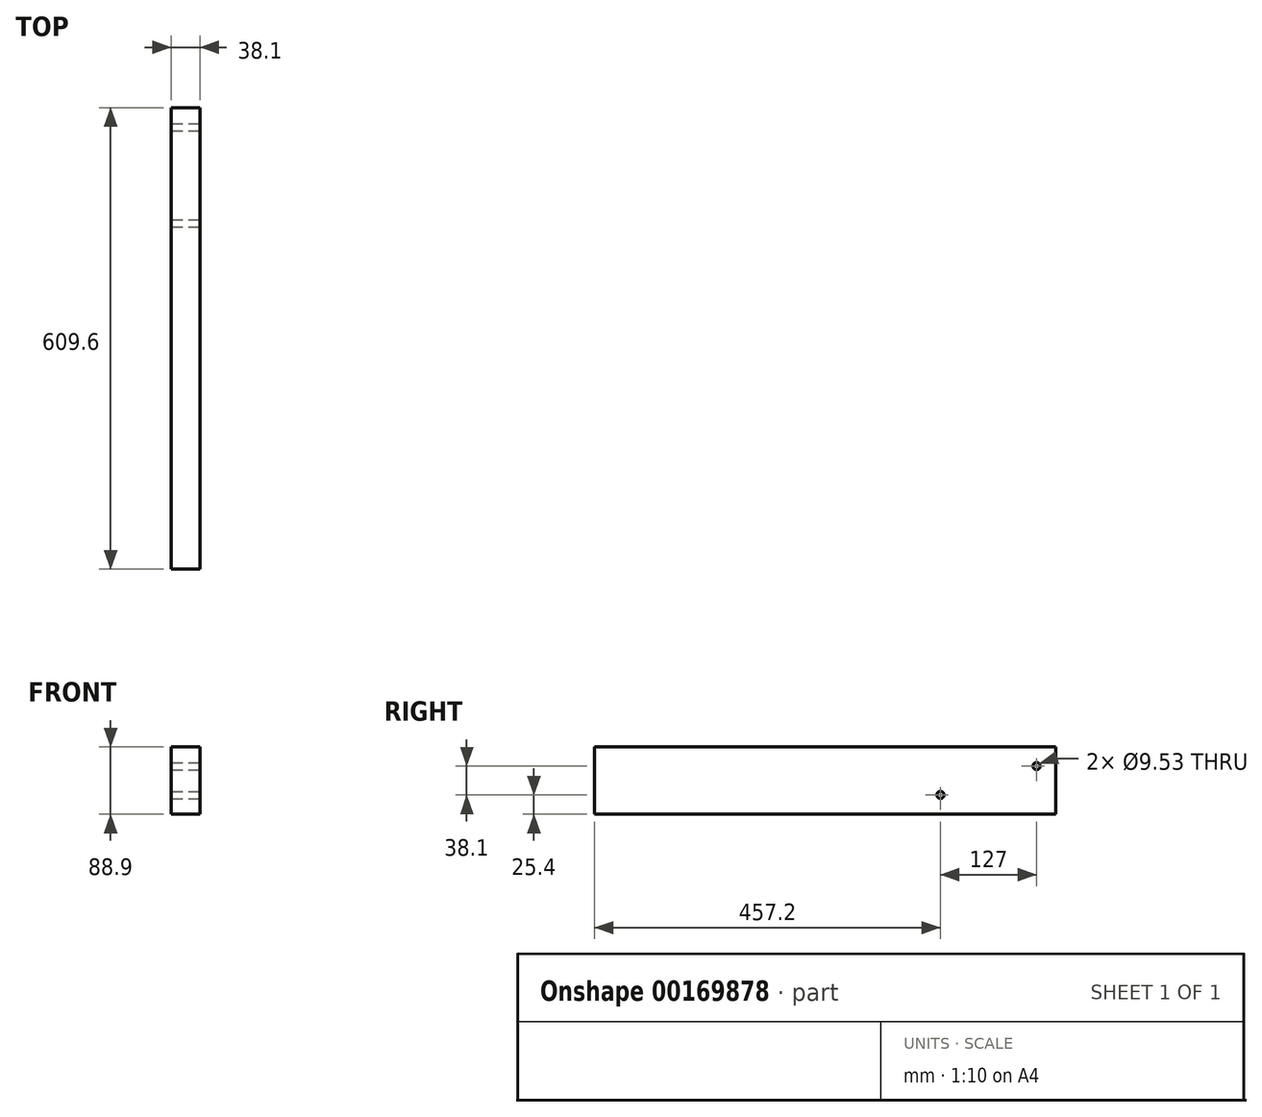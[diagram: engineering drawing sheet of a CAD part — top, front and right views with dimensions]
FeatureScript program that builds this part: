
annotation { "Feature Type Name" : "Feature", "Feature Type Description" : "" }
export const myFeature = defineFeature(function(context is Context, id is Id, definition is map)
    precondition{}
    {
        {
            var Q0;
            Q0=qCreatedBy(makeId("Right.planeOp"),FACE);
            var sketch = newSketch(context, id + "F0", { "sketchPlane" : qUnion([Q0])});
            skLineSegment(sketch, "E0.bottom", {"start": v(0, 0) * mm, "end": v(609.6, 0) * mm});
            skLineSegment(sketch, "E0.top", {"start": v(0, 88.9) * mm, "end": v(609.6, 88.9) * mm});
            skLineSegment(sketch, "E0.left", {"start": v(0, 0) * mm, "end": v(0, 88.9) * mm});
            skLineSegment(sketch, "E0.right", {"start": v(609.6, 0) * mm, "end": v(609.6, 88.9) * mm});
            skSolve(sketch);
        }
        {
            var Q0;
            Q0 = qSketchRegion(id + "F0", true);
            extrude(context, id + "F1", {"entities" : qUnion([Q0]), "depth" : 38.1 * mm});
        }
        {
            var Q0;
            Q0=makeQuery(id+"F1.opExtrude","CAP_FACE",FACE,{"disambiguationData":[OSD([sQuery(id+"F0.wireOp",EDGE,"E0.bottom"),sQuery(id+"F0.wireOp",EDGE,"E0.top"),sQuery(id+"F0.wireOp",EDGE,"E0.left"),sQuery(id+"F0.wireOp",EDGE,"E0.right")])],"isStart":false});
            var sketch = newSketch(context, id + "F2", { "sketchPlane" : qUnion([Q0])});
            skCircle(sketch, "E1", {"center": v(457.2, 25.4) * mm, "radius": 4.76 * mm});
            skLineSegment(sketch, "E2", {"start": v(457.2, 25.4) * mm, "end": v(609.6, 25.4) * mm, "construction": true});
            skLineSegment(sketch, "E3", {"start": v(457.2, 25.4) * mm, "end": v(457.2, 0) * mm, "construction": true});
            skLineSegment(sketch, "E4", {"start": v(584.2, 88.9) * mm, "end": v(584.2, 63.5) * mm, "construction": true});
            skLineSegment(sketch, "E5", {"start": v(584.2, 63.5) * mm, "end": v(609.6, 63.5) * mm, "construction": true});
            skCircle(sketch, "E6", {"center": v(584.2, 63.5) * mm, "radius": 4.76 * mm});
            skSolve(sketch);
        }
        {
            var Q0;
            Q0 = qSketchRegion(id + "F2", true);
            extrude(context, id + "F3", {"entities" : qUnion([Q0]), "operationType" : NewBodyOperationType.REMOVE, "endBound" : BoundingType.THROUGH_ALL, "oppositeDirection" : true, "depth" : 25.4 * mm});
        }
    });
